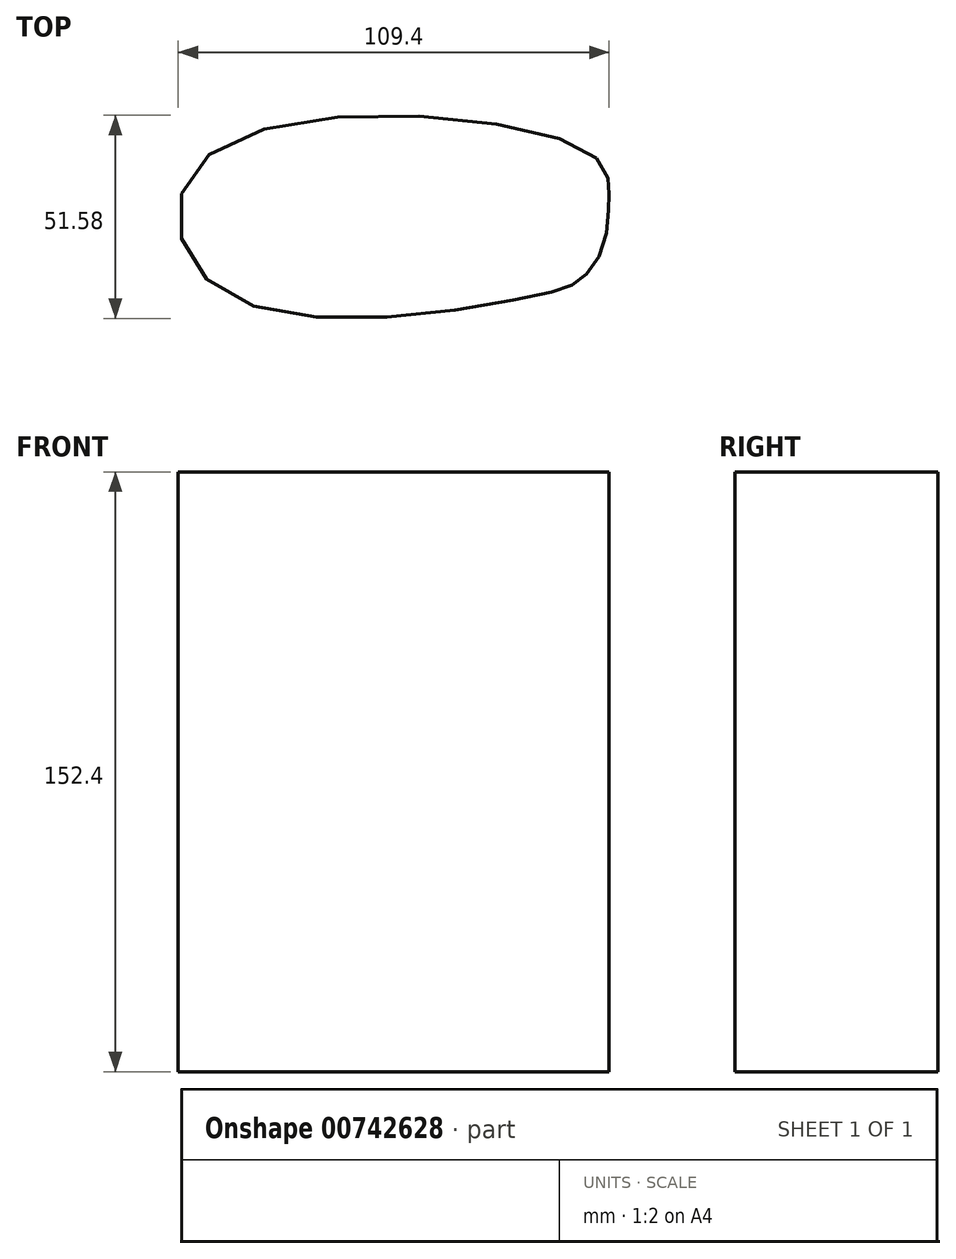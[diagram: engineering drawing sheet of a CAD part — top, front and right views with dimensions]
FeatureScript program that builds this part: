
annotation { "Feature Type Name" : "Feature", "Feature Type Description" : "" }
export const myFeature = defineFeature(function(context is Context, id is Id, definition is map)
    precondition{}
    {
        {
            var Q0;
            Q0=qCreatedBy(makeId("Top.planeOp"),FACE);
            var sketch = newSketch(context, id + "F0", { "sketchPlane" : qUnion([Q0])});
            skFitSpline(sketch, "E0", {"points": [v(-51.74, 13.2) * mm, v(44.1, 14.25) * mm, v(49.83, 4.88) * mm, v(49.8, 0) * mm, v(48.02, -11.27) * mm, v(42.3, -18.75) * mm, v(31.4, -22.58) * mm, v(-48.14, -21.75) * mm, v(-51.74, 13.2) * mm]});
            skSolve(sketch);
        }
        {
            var Q0;
            Q0=sQuery(id+"F0.wireOp",EDGE,"E0");
            extrude(context, id + "F1", {"bodyType" : ToolBodyType.SURFACE, "surfaceEntities" : qUnion([Q0]), "depth" : 152.4 * mm, "offsetDistance" : 25.4 * mm});
        }
    });
